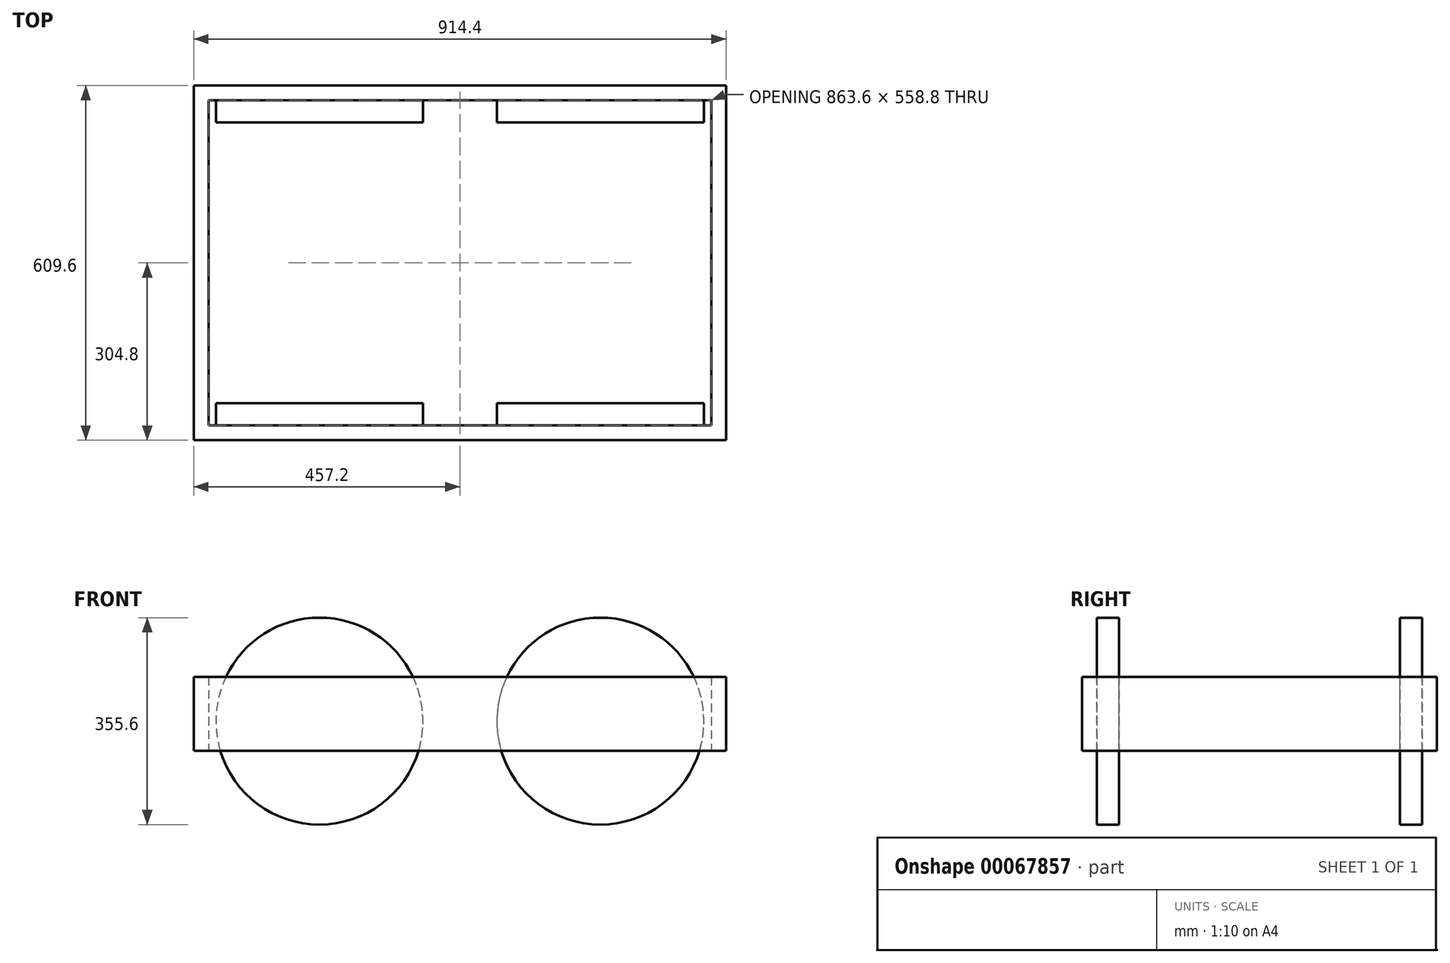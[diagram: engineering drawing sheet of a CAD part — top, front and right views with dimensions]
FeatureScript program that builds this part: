
annotation { "Feature Type Name" : "Feature", "Feature Type Description" : "" }
export const myFeature = defineFeature(function(context is Context, id is Id, definition is map)
    precondition{}
    {
        {
            var Q0;
            Q0=qCreatedBy(makeId("Top.planeOp"),FACE);
            var sketch = newSketch(context, id + "F0", { "sketchPlane" : qUnion([Q0])});
            skLineSegment(sketch, "E0.rect.bottom", {"start": v(457.2, -304.8) * mm, "end": v(-457.2, -304.8) * mm});
            skLineSegment(sketch, "E0.rect.top", {"start": v(457.2, 304.8) * mm, "end": v(-457.2, 304.8) * mm});
            skLineSegment(sketch, "E0.rect.left", {"start": v(457.2, -304.8) * mm, "end": v(457.2, 304.8) * mm});
            skLineSegment(sketch, "E0.rect.right", {"start": v(-457.2, -304.8) * mm, "end": v(-457.2, 304.8) * mm});
            skPoint(sketch, "E0.rect.middle", {"position": v(0, 0) * mm});
            skLineSegment(sketch, "E1.0", {"start": v(-431.8, -279.4) * mm, "end": v(-431.8, 279.4) * mm});
            skLineSegment(sketch, "E1.1", {"start": v(431.8, -279.4) * mm, "end": v(-431.8, -279.4) * mm});
            skLineSegment(sketch, "E1.2", {"start": v(431.8, -279.4) * mm, "end": v(431.8, 279.4) * mm});
            skLineSegment(sketch, "E1.3", {"start": v(431.8, 279.4) * mm, "end": v(-431.8, 279.4) * mm});
            skSolve(sketch);
        }
        {
            var Q0;
            Q0 = qSketchRegion(id + "F0", true);
            extrude(context, id + "F1", {"entities" : qUnion([Q0]), "depth" : 127 * mm});
        }
        {
            var Q0;
            Q0=makeQuery(id+"F1.opExtrude","SWEPT_FACE",FACE,{"disambiguationData":[OSD([sQuery(id+"F0.wireOp",EDGE,"E1.3")])]});
            var sketch = newSketch(context, id + "F2", { "sketchPlane" : qUnion([Q0])});
            skCircle(sketch, "E2", {"center": v(-241.3, 50.8) * mm, "radius": 177.8 * mm});
            skLineSegment(sketch, "E3", {"start": v(0, -127) * mm, "end": v(-437.6, -127) * mm, "construction": true});
            skLineSegment(sketch, "E4.1", {"start": v(457.2, 0) * mm, "end": v(-457.2, 0) * mm, "construction": true});
            skLineSegment(sketch, "E5.0", {"start": v(-431.8, 127) * mm, "end": v(-431.8, 0) * mm, "construction": true});
            skLineSegment(sketch, "E6", {"start": v(-419.1, 127) * mm, "end": v(-419.1, 0) * mm, "construction": true});
            skLineSegment(sketch, "E7", {"start": v(0, 0) * mm, "end": v(0, 127) * mm, "construction": true});
            skCircle(sketch, "E8.MirrorC", {"center": v(241.3, 50.8) * mm, "radius": 177.8 * mm});
            skSolve(sketch);
        }
        {
            var Q0;
            Q0 = qSketchRegion(id + "F2", true);
            extrude(context, id + "F3", {"entities" : qUnion([Q0]), "depth" : 38.1 * mm});
        }
        {
            var Q0;
            Q0=makeQuery(id+"F3.opExtrude","SWEPT_BODY",BODY,{"disambiguationData":[OSD([sQuery(id+"F2.wireOp",EDGE,"E2")])]});
            var Q1;
            Q1=makeQuery(id+"F3.opExtrude","SWEPT_BODY",BODY,{"disambiguationData":[OSD([sQuery(id+"F2.wireOp",EDGE,"E8.MirrorC")])]});
            var Q2;
            Q2=qCreatedBy(makeId("Front.planeOp"),FACE);
            mirror(context, id + "F4", {"operationType" : NewBodyOperationType.ADD, "entities" : qUnion([Q0, Q1]), "mirrorPlane" : qUnion([Q2])});
        }
    });
